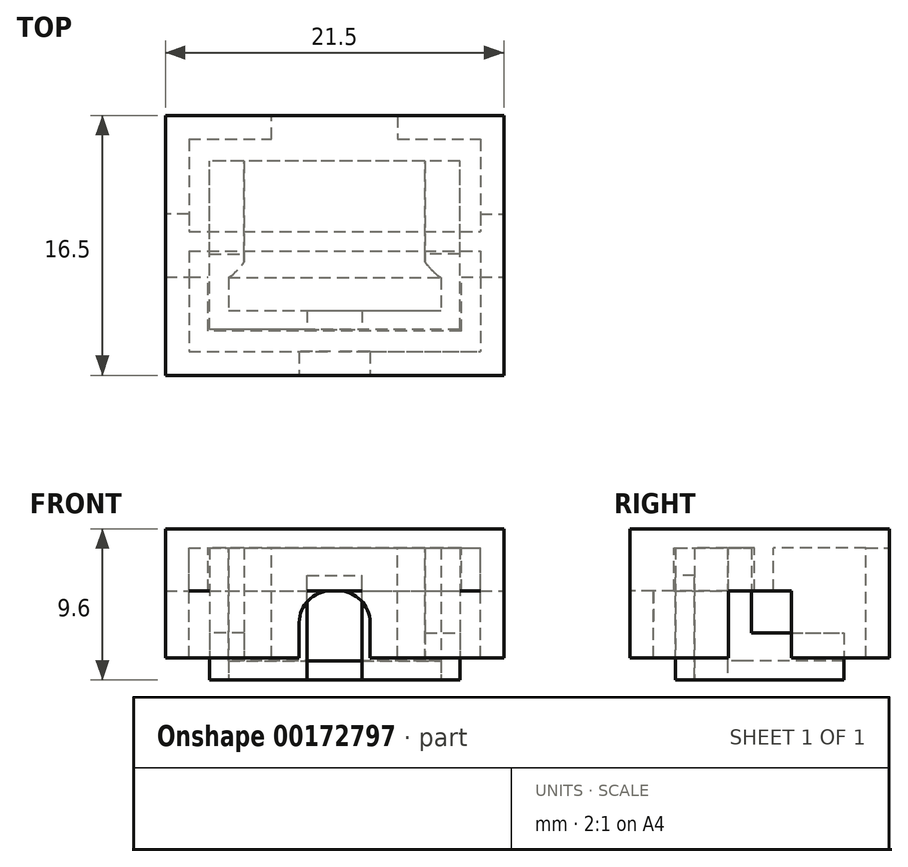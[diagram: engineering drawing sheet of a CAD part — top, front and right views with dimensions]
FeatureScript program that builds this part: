
annotation { "Feature Type Name" : "Feature", "Feature Type Description" : "" }
export const myFeature = defineFeature(function(context is Context, id is Id, definition is map)
    precondition{}
    {
        {
            var Q0;
            Q0=qCreatedBy(makeId("Top.planeOp"),FACE);
            var sketch = newSketch(context, id + "F0", { "sketchPlane" : qUnion([Q0])});
            skLineSegment(sketch, "E0.bottom", {"start": v(-6.75, 1.05) * mm, "end": v(6.75, 1.05) * mm});
            skLineSegment(sketch, "E0.top", {"start": v(-6.75, -1.05) * mm, "end": v(6.75, -1.05) * mm});
            skLineSegment(sketch, "E0.left", {"start": v(-6.75, 1.05) * mm, "end": v(-6.75, -1.05) * mm});
            skLineSegment(sketch, "E0.right", {"start": v(6.75, 1.05) * mm, "end": v(6.75, -1.05) * mm});
            skPoint(sketch, "E0.middle", {"position": v(0, 0) * mm});
            skLineSegment(sketch, "E1.bottom", {"start": v(7.95, -2.26) * mm, "end": v(-7.95, -2.26) * mm});
            skLineSegment(sketch, "E1.top", {"start": v(7.95, 8.44) * mm, "end": v(-7.95, 8.44) * mm});
            skLineSegment(sketch, "E1.left", {"start": v(7.95, -2.26) * mm, "end": v(7.95, 8.44) * mm});
            skLineSegment(sketch, "E1.right", {"start": v(-7.95, -2.26) * mm, "end": v(-7.95, 8.44) * mm});
            skPoint(sketch, "E2", {"position": v(0, -2.26) * mm});
            skLineSegment(sketch, "E3", {"start": v(-6.75, 1.05) * mm, "end": v(-6.75, 7.24) * mm});
            skLineSegment(sketch, "E4", {"start": v(-6.75, 7.24) * mm, "end": v(6.75, 7.24) * mm});
            skLineSegment(sketch, "E5", {"start": v(6.75, 7.24) * mm, "end": v(6.75, 1.05) * mm});
            skLineSegment(sketch, "E6", {"start": v(-5.75, 1.05) * mm, "end": v(-5.75, 2.55) * mm});
            skLineSegment(sketch, "E7", {"start": v(-5.75, 2.55) * mm, "end": v(-6.75, 2.55) * mm});
            skLineSegment(sketch, "E8", {"start": v(5.75, 1.05) * mm, "end": v(5.75, 2.55) * mm});
            skLineSegment(sketch, "E9", {"start": v(5.75, 2.55) * mm, "end": v(6.75, 2.55) * mm});
            skLineSegment(sketch, "E10", {"start": v(7.95, 2.55) * mm, "end": v(6.75, 2.55) * mm});
            skLineSegment(sketch, "E11", {"start": v(-7.95, 2.55) * mm, "end": v(-6.75, 2.55) * mm});
            skLineSegment(sketch, "E12", {"start": v(-5.75, 2.55) * mm, "end": v(-5.75, 8.44) * mm});
            skLineSegment(sketch, "E13", {"start": v(5.75, 2.55) * mm, "end": v(5.75, 8.44) * mm});
            skSolve(sketch);
        }
        {
            var Q0;
            Q0=makeQuery(id+"F0.imprint","IMPRINT",FACE,{"disambiguationData":[TD([[makeQuery(id+"F0.imprint","IMPRINT",EDGE,{"derivedFrom":sQuery(id+"F0.wireOp",EDGE,"E0.bottom")}),1.0]])]});
            var Q1;
            {var subQ1=sQuery(id+"F0.wireOp",EDGE,"E4");Q1=makeQuery(id+"F0.imprint","IMPRINT",FACE,{"disambiguationData":[TD([[makeQuery(id+"F0.imprint","IMPRINT",EDGE,{"derivedFrom":subQ1}),-1.0]])]});}
            var Q2;
            {var subQ4=sQuery(id+"F0.wireOp",EDGE,"E1.top");Q2=makeQuery(id+"F0.imprint","IMPRINT",FACE,{"disambiguationData":[TD([[makeQuery(id+"F0.imprint","IMPRINT",EDGE,{"derivedFrom":subQ4}),1.0]])]});}
            var Q3;
            Q3=makeQuery(id+"F0.imprint","IMPRINT",FACE,{"disambiguationData":[TD([[makeQuery(id+"F0.imprint","IMPRINT",EDGE,{"derivedFrom":sQuery(id+"F0.wireOp",EDGE,"E0.top")}),-1.0]])]});
            var Q4;
            {var subQ4=sQuery(id+"F0.wireOp",EDGE,"E11");Q4=makeQuery(id+"F0.imprint","IMPRINT",FACE,{"disambiguationData":[TD([[makeQuery(id+"F0.imprint","IMPRINT",EDGE,{"derivedFrom":subQ4}),1.0]])]});}
            var Q5;
            {var subQ7=sQuery(id+"F0.wireOp",EDGE,"E10");Q5=makeQuery(id+"F0.imprint","IMPRINT",FACE,{"disambiguationData":[TD([[makeQuery(id+"F0.imprint","IMPRINT",EDGE,{"derivedFrom":subQ7}),-1.0]])]});}
            var Q6;
            {var subQ0=sQuery(id+"F0.wireOp",EDGE,"E6");Q6=makeQuery(id+"F0.imprint","IMPRINT",FACE,{"disambiguationData":[TD([[makeQuery(id+"F0.imprint","IMPRINT",EDGE,{"derivedFrom":subQ0}),-1.0]])]});}
            extrude(context, id + "F1", {"entities" : qUnion([Q0, Q1, Q2, Q3, Q4, Q5, Q6]), "depth" : 1.21 * mm});
        }
        {
            var Q0;
            Q0=makeQuery(id+"F0.imprint","IMPRINT",FACE,{"disambiguationData":[TD([[makeQuery(id+"F0.imprint","IMPRINT",EDGE,{"derivedFrom":sQuery(id+"F0.wireOp",EDGE,"E0.top")}),-1.0]])]});
            var Q1;
            {var subQ3=sQuery(id+"F0.wireOp",EDGE,"E6");Q1=makeQuery(id+"F0.imprint","IMPRINT",FACE,{"disambiguationData":[TD([[makeQuery(id+"F0.imprint","IMPRINT",EDGE,{"derivedFrom":subQ3}),1.0]])]});}
            var Q2;
            {var subQ3=sQuery(id+"F0.wireOp",EDGE,"E8");Q2=makeQuery(id+"F0.imprint","IMPRINT",FACE,{"disambiguationData":[TD([[makeQuery(id+"F0.imprint","IMPRINT",EDGE,{"derivedFrom":subQ3}),-1.0]])]});}
            extrude(context, id + "F2", {"entities" : qUnion([Q0, Q1, Q2]), "depth" : 8.4 * mm});
        }
        {
            var Q0;
            Q0=makeQuery(id+"F1.opExtrude","SWEPT_BODY",BODY,{"disambiguationData":[OSD([sQuery(id+"F0.wireOp",EDGE,"E1.bottom"),sQuery(id+"F0.wireOp",EDGE,"E1.top"),sQuery(id+"F0.wireOp",EDGE,"E1.left"),sQuery(id+"F0.wireOp",EDGE,"E1.right")])]});
            var Q1;
            Q1=makeQuery(id+"F2.opExtrude","SWEPT_BODY",BODY,{"disambiguationData":[OSD([sQuery(id+"F0.wireOp",EDGE,"E0.bottom"),sQuery(id+"F0.wireOp",EDGE,"E0.top"),sQuery(id+"F0.wireOp",EDGE,"E0.left"),sQuery(id+"F0.wireOp",EDGE,"E0.right"),sQuery(id+"F0.wireOp",EDGE,"E1.bottom"),sQuery(id+"F0.wireOp",EDGE,"E1.left"),sQuery(id+"F0.wireOp",EDGE,"E1.right"),sQuery(id+"F0.wireOp",EDGE,"E6"),sQuery(id+"F0.wireOp",EDGE,"E7"),sQuery(id+"F0.wireOp",EDGE,"E8"),sQuery(id+"F0.wireOp",EDGE,"E9"),sQuery(id+"F0.wireOp",EDGE,"E10"),sQuery(id+"F0.wireOp",EDGE,"E11")])]});
            booleanBodies(context, id + "F3", {"operationType" : BooleanOperationType.UNION, "tools" : qUnion([Q0, Q1])});
        }
        {
            var Q0;
            Q0=makeQuery(id+"F2.opExtrude","SWEPT_FACE",FACE,{"disambiguationData":[OSD([sQuery(id+"F0.wireOp",EDGE,"E1.bottom")])]});
            var sketch = newSketch(context, id + "F4", { "sketchPlane" : qUnion([Q0])});
            skLineSegment(sketch, "E14.bottom", {"start": v(-1.75, 0) * mm, "end": v(1.75, 0) * mm});
            skLineSegment(sketch, "E14.top", {"start": v(-1.75, 6.65) * mm, "end": v(1.75, 6.65) * mm});
            skLineSegment(sketch, "E14.left", {"start": v(-1.75, 0) * mm, "end": v(-1.75, 6.65) * mm});
            skLineSegment(sketch, "E14.right", {"start": v(1.75, 0) * mm, "end": v(1.75, 6.65) * mm});
            skSolve(sketch);
        }
        {
            var Q0;
            Q0 = qSketchRegion(id + "F4", true);
            var Q1;
            Q1=makeQuery(id+"F2.opExtrude","SWEPT_FACE",FACE,{"disambiguationData":[OSD([sQuery(id+"F0.wireOp",EDGE,"E0.top")])]});
            extrude(context, id + "F5", {"entities" : qUnion([Q0]), "operationType" : NewBodyOperationType.REMOVE, "endBound" : BoundingType.UP_TO_SURFACE, "oppositeDirection" : true, "endBoundEntityFace" : qUnion([Q1]), "depth" : 25 * mm});
        }
        {
            var Q0;
            Q0=makeQuery(id+"F2.opExtrude","SWEPT_EDGE",EDGE,{"disambiguationData":[OSD([sQuery(id+"F0.wireOp",EDGE,"E0.bottom"),sQuery(id+"F0.wireOp",EDGE,"E8")])]});
            var Q1;
            Q1=makeQuery(id+"F2.opExtrude","SWEPT_EDGE",EDGE,{"disambiguationData":[OSD([sQuery(id+"F0.wireOp",EDGE,"E0.bottom"),sQuery(id+"F0.wireOp",EDGE,"E6")])]});
            fillet(context, id + "F6", {"entities" : qUnion([Q0, Q1]), "radius" : 1 * mm, "tangentPropagation" : true, "rho" : .1, "crossSection" : FilletCrossSection.CONIC, "allowEdgeOverflow" : false});
        }
        {
            var Q0;
            {var subQ5=sQuery(id+"F0.wireOp",EDGE,"E11");Q0=makeQuery(id+"F0.imprint","IMPRINT",FACE,{"disambiguationData":[TD([[makeQuery(id+"F0.imprint","IMPRINT",EDGE,{"derivedFrom":subQ5}),1.0]])]});}
            var Q1;
            {var subQ3=sQuery(id+"F0.wireOp",EDGE,"E7");Q1=makeQuery(id+"F0.imprint","IMPRINT",FACE,{"disambiguationData":[TD([[makeQuery(id+"F0.imprint","IMPRINT",EDGE,{"derivedFrom":subQ3}),-1.0]])]});}
            var Q2;
            {var subQ5=sQuery(id+"F0.wireOp",EDGE,"E9");Q2=makeQuery(id+"F0.imprint","IMPRINT",FACE,{"disambiguationData":[TD([[makeQuery(id+"F0.imprint","IMPRINT",EDGE,{"derivedFrom":subQ5}),1.0]])]});}
            var Q3;
            {var subQ9=sQuery(id+"F0.wireOp",EDGE,"E10");Q3=makeQuery(id+"F0.imprint","IMPRINT",FACE,{"disambiguationData":[TD([[makeQuery(id+"F0.imprint","IMPRINT",EDGE,{"derivedFrom":subQ9}),-1.0]])]});}
            extrude(context, id + "F7", {"entities" : qUnion([Q0, Q1, Q2, Q3]), "operationType" : NewBodyOperationType.ADD, "depth" : 3 * mm});
        }
        {
            var Q0;
            Q0=makeQuery(id+"F2.opExtrude","CAP_FACE",FACE,{"disambiguationData":[OSD([sQuery(id+"F0.wireOp",EDGE,"E0.bottom"),sQuery(id+"F0.wireOp",EDGE,"E0.top"),sQuery(id+"F0.wireOp",EDGE,"E0.left"),sQuery(id+"F0.wireOp",EDGE,"E0.right"),sQuery(id+"F0.wireOp",EDGE,"E1.bottom"),sQuery(id+"F0.wireOp",EDGE,"E1.left"),sQuery(id+"F0.wireOp",EDGE,"E1.right"),sQuery(id+"F0.wireOp",EDGE,"E6"),sQuery(id+"F0.wireOp",EDGE,"E7"),sQuery(id+"F0.wireOp",EDGE,"E8"),sQuery(id+"F0.wireOp",EDGE,"E9"),sQuery(id+"F0.wireOp",EDGE,"E10"),sQuery(id+"F0.wireOp",EDGE,"E11")])],"isStart":false});
            var sketch = newSketch(context, id + "F8", { "sketchPlane" : qUnion([Q0])});
            skLineSegment(sketch, "E15.bottom", {"start": v(-9.25, 9.84) * mm, "end": v(9.25, 9.84) * mm});
            skLineSegment(sketch, "E15.top", {"start": v(-9.25, -3.66) * mm, "end": v(-2.25, -3.66) * mm});
            skLineSegment(sketch, "E15.left", {"start": v(-9.25, 9.84) * mm, "end": v(-9.25, 5.1) * mm});
            skLineSegment(sketch, "E15.right", {"start": v(9.25, 9.84) * mm, "end": v(9.25, -3.66) * mm});
            skPoint(sketch, "E15.middle", {"position": v(0, 3.1) * mm});
            skLineSegment(sketch, "E16.0", {"start": v(-10.75, 11.34) * mm, "end": v(-10.75, -5.16) * mm});
            skLineSegment(sketch, "E16.1", {"start": v(-10.75, 11.34) * mm, "end": v(-4, 11.34) * mm});
            skLineSegment(sketch, "E16.2", {"start": v(10.75, 11.34) * mm, "end": v(10.75, -5.16) * mm});
            skLineSegment(sketch, "E16.3", {"start": v(-10.75, -5.16) * mm, "end": v(10.75, -5.16) * mm});
            skLineSegment(sketch, "E17", {"start": v(-9.25, 5.1) * mm, "end": v(-10.75, 5.1) * mm});
            skLineSegment(sketch, "E18", {"start": v(-10.75, 1.1) * mm, "end": v(-7.95, 1.1) * mm});
            skLineSegment(sketch, "E19", {"start": v(-9.25, 5.1) * mm, "end": v(-9.25, 1.1) * mm});
            skLineSegment(sketch, "E20", {"start": v(-9.25, 1.1) * mm, "end": v(-9.25, -3.66) * mm});
            skPoint(sketch, "E21", {"position": v(-9.25, 3.1) * mm});
            skLineSegment(sketch, "E22", {"start": v(9.25, 5.1) * mm, "end": v(10.75, 5.1) * mm});
            skLineSegment(sketch, "E23", {"start": v(7.95, 1.1) * mm, "end": v(10.75, 1.1) * mm});
            skLineSegment(sketch, "E24", {"start": v(-9.25, 2.55) * mm, "end": v(9.25, 2.55) * mm, "construction": true});
            skLineSegment(sketch, "E25", {"start": v(-9.25, 3.96) * mm, "end": v(9.25, 3.96) * mm});
            skLineSegment(sketch, "E26.0", {"start": v(-7.95, -2.26) * mm, "end": v(-7.95, 2.55) * mm, "construction": true});
            skLineSegment(sketch, "E26.1", {"start": v(7.95, -2.26) * mm, "end": v(-7.95, -2.26) * mm, "construction": true});
            skLineSegment(sketch, "E26.2", {"start": v(7.95, -2.26) * mm, "end": v(7.95, 2.55) * mm, "construction": true});
            skLineSegment(sketch, "E27", {"start": v(-4, 9.84) * mm, "end": v(-4, 11.34) * mm});
            skLineSegment(sketch, "E28", {"start": v(4, 11.34) * mm, "end": v(4, 9.84) * mm});
            skLineSegment(sketch, "E29", {"start": v(-4, 11.34) * mm, "end": v(4, 11.34) * mm});
            skLineSegment(sketch, "E30", {"start": v(4, 11.34) * mm, "end": v(10.75, 11.34) * mm});
            skPoint(sketch, "E31", {"position": v(0, 11.34) * mm});
            skPoint(sketch, "E32.orphan", {"position": v(-9.25, 1.1) * mm});
            skPoint(sketch, "E33.orphan", {"position": v(9.25, 1.1) * mm});
            skLineSegment(sketch, "E34", {"start": v(-2.25, -3.66) * mm, "end": v(2.25, -3.66) * mm});
            skLineSegment(sketch, "E35", {"start": v(2.25, -3.66) * mm, "end": v(9.25, -3.66) * mm});
            skPoint(sketch, "E36", {"position": v(0, -3.66) * mm});
            skLineSegment(sketch, "E37.0", {"start": v(-9.25, 2.75) * mm, "end": v(9.25, 2.75) * mm});
            skLineSegment(sketch, "E38.0", {"start": v(-8.05, -2.36) * mm, "end": v(-8.05, 2.55) * mm});
            skLineSegment(sketch, "E38.1", {"start": v(8.05, -2.36) * mm, "end": v(-8.05, -2.36) * mm});
            skLineSegment(sketch, "E38.2", {"start": v(8.05, -2.36) * mm, "end": v(8.05, 2.55) * mm});
            skSolve(sketch);
        }
        {
            var Q0;
            {var subQ6=sQuery(id+"F8.wireOp",EDGE,"E15.top");Q0=makeQuery(id+"F8.imprint","IMPRINT",FACE,{"disambiguationData":[TD([[makeQuery(id+"F8.imprint","IMPRINT",EDGE,{"derivedFrom":subQ6}),-1.0]])]});}
            var Q1;
            {var subQ1=sQuery(id+"F8.wireOp",EDGE,"E15.left");Q1=makeQuery(id+"F8.imprint","IMPRINT",FACE,{"disambiguationData":[TD([[makeQuery(id+"F8.imprint","IMPRINT",EDGE,{"derivedFrom":subQ1}),-1.0]])]});}
            var Q2;
            {var subQ0=sQuery(id+"F8.wireOp",EDGE,"E22");Q2=makeQuery(id+"F8.imprint","IMPRINT",FACE,{"disambiguationData":[TD([[makeQuery(id+"F8.imprint","IMPRINT",EDGE,{"derivedFrom":subQ0}),1.0]])]});}
            var Q3;
            {var subQ5=sQuery(id+"F8.wireOp",EDGE,"J5TBD8wA-XzV8-tCQy-03cy-WX8Owma7t69J");Q3=makeQuery(id+"F8.imprint","IMPRINT",FACE,{"disambiguationData":[TD([[makeQuery(id+"F8.imprint","IMPRINT",EDGE,{"derivedFrom":subQ5}),-1.0]])]});}
            var Q4;
            Q4=makeQuery(id+"F1.opExtrude","CAP_FACE",FACE,{"disambiguationData":[OSD([sQuery(id+"F0.wireOp",EDGE,"E0.bottom"),sQuery(id+"F0.wireOp",EDGE,"E0.top"),sQuery(id+"F0.wireOp",EDGE,"E0.left"),sQuery(id+"F0.wireOp",EDGE,"E0.right"),sQuery(id+"F0.wireOp",EDGE,"E1.bottom"),sQuery(id+"F0.wireOp",EDGE,"E1.top"),sQuery(id+"F0.wireOp",EDGE,"E1.left"),sQuery(id+"F0.wireOp",EDGE,"E1.right")])],"isStart":false});
            extrude(context, id + "F9", {"entities" : qUnion([Q0, Q1, Q2, Q3]), "oppositeDirection" : true, "endBoundEntityFace" : qUnion([Q4]), "depth" : 7 * mm});
        }
        {
            var Q0;
            {var subQ0=sQuery(id+"F8.wireOp",EDGE,"E38.1");Q0=makeQuery(id+"F8.imprint","IMPRINT",FACE,{"disambiguationData":[TD([[makeQuery(id+"F8.imprint","IMPRINT",EDGE,{"derivedFrom":subQ0}),-1.0]])]});}
            var Q1;
            {var subQ2=sQuery(id+"F8.wireOp",EDGE,"E37.0");Q1=makeQuery(id+"F8.imprint","IMPRINT",FACE,{"disambiguationData":[TD([[makeQuery(id+"F8.imprint","IMPRINT",EDGE,{"derivedFrom":subQ2}),-1.0]])]});}
            var Q2;
            {var subQ11=sQuery(id+"F0.wireOp",EDGE,"E0.top");Q2=makeQuery(id+"F8.imprint","IMPRINT",FACE,{"disambiguationData":[TD([[makeQuery(id+"F8.imprint","IMPRINT",EDGE,{"derivedFrom":makeQuery(id+"F2.opExtrude","CAP_EDGE",EDGE,{"disambiguationData":[OSD([subQ11])],"isStart":false})}),-1.0]])]});}
            var Q3;
            {var subQ1=sQuery(id+"F8.wireOp",EDGE,"E17");Q3=makeQuery(id+"F8.imprint","IMPRINT",FACE,{"disambiguationData":[TD([[makeQuery(id+"F8.imprint","IMPRINT",EDGE,{"derivedFrom":subQ1}),1.0]])]});}
            var Q4;
            Q4=makeQuery(id+"F8.imprint","IMPRINT",FACE,{"disambiguationData":[TD([[makeQuery(id+"F8.imprint","IMPRINT",EDGE,{"derivedFrom":sQuery(id+"F8.wireOp",EDGE,"E15.top")}),-1.0]])]});
            var Q5;
            Q5=makeQuery(id+"F8.imprint","IMPRINT",FACE,{"disambiguationData":[TD([[makeQuery(id+"F8.imprint","IMPRINT",EDGE,{"derivedFrom":sQuery(id+"F8.wireOp",EDGE,"E15.top")}),1.0]])]});
            var Q6;
            {var subQ0=sQuery(id+"F8.wireOp",EDGE,"E22");Q6=makeQuery(id+"F8.imprint","IMPRINT",FACE,{"disambiguationData":[TD([[makeQuery(id+"F8.imprint","IMPRINT",EDGE,{"derivedFrom":subQ0}),-1.0]])]});}
            var Q7;
            {var subQ0=sQuery(id+"F8.wireOp",EDGE,"E25");Q7=makeQuery(id+"F8.imprint","IMPRINT",FACE,{"disambiguationData":[TD([[makeQuery(id+"F8.imprint","IMPRINT",EDGE,{"derivedFrom":subQ0}),-1.0]])]});}
            var Q8;
            {var subQ0=sQuery(id+"F8.wireOp",EDGE,"E15.left");Q8=makeQuery(id+"F8.imprint","IMPRINT",FACE,{"disambiguationData":[TD([[makeQuery(id+"F8.imprint","IMPRINT",EDGE,{"derivedFrom":subQ0}),1.0]])]});}
            var Q9;
            {var subQ1=sQuery(id+"F8.wireOp",EDGE,"E15.left");Q9=makeQuery(id+"F8.imprint","IMPRINT",FACE,{"disambiguationData":[TD([[makeQuery(id+"F8.imprint","IMPRINT",EDGE,{"derivedFrom":subQ1}),-1.0]])]});}
            var Q10;
            {var subQ0=sQuery(id+"F8.wireOp",EDGE,"E27");Q10=makeQuery(id+"F8.imprint","IMPRINT",FACE,{"disambiguationData":[TD([[makeQuery(id+"F8.imprint","IMPRINT",EDGE,{"derivedFrom":subQ0}),-1.0]])]});}
            var Q11;
            {var subQ0=sQuery(id+"F8.wireOp",EDGE,"E22");Q11=makeQuery(id+"F8.imprint","IMPRINT",FACE,{"disambiguationData":[TD([[makeQuery(id+"F8.imprint","IMPRINT",EDGE,{"derivedFrom":subQ0}),1.0]])]});}
            extrude(context, id + "F10", {"entities" : qUnion([Q0, Q1, Q2, Q3, Q4, Q5, Q6, Q7, Q8, Q9, Q10, Q11]), "operationType" : NewBodyOperationType.ADD, "depth" : 1.2 * mm});
        }
        {
            var Q0;
            {var subQ1=sQuery(id+"F8.wireOp",EDGE,"E17");Q0=makeQuery(id+"F8.imprint","IMPRINT",FACE,{"disambiguationData":[TD([[makeQuery(id+"F8.imprint","IMPRINT",EDGE,{"derivedFrom":subQ1}),1.0]])]});}
            var Q1;
            {var subQ0=sQuery(id+"F8.wireOp",EDGE,"E25");Q1=makeQuery(id+"F8.imprint","IMPRINT",FACE,{"disambiguationData":[TD([[makeQuery(id+"F8.imprint","IMPRINT",EDGE,{"derivedFrom":subQ0}),-1.0]])]});}
            var Q2;
            {var subQ0=sQuery(id+"F8.wireOp",EDGE,"E22");Q2=makeQuery(id+"F8.imprint","IMPRINT",FACE,{"disambiguationData":[TD([[makeQuery(id+"F8.imprint","IMPRINT",EDGE,{"derivedFrom":subQ0}),-1.0]])]});}
            var Q3;
            Q3=makeQuery(id+"F8.imprint","IMPRINT",FACE,{"disambiguationData":[TD([[makeQuery(id+"F8.imprint","IMPRINT",EDGE,{"derivedFrom":sQuery(id+"F8.wireOp",EDGE,"E15.top")}),1.0]])]});
            extrude(context, id + "F11", {"entities" : qUnion([Q0, Q1, Q2, Q3]), "operationType" : NewBodyOperationType.ADD, "oppositeDirection" : true, "depth" : 2.75 * mm});
        }
        {
            var Q0;
            {var subQ0=sQuery(id+"F8.wireOp",EDGE,"E16.3");Q0=makeQuery(id+"F10.boolean.opBoolean","MERGE",FACE,{"derivedFrom":[makeQuery(id+"F9.opExtrude","SWEPT_FACE",FACE,{"disambiguationData":[OSD([subQ0])]}),makeQuery(id+"F10.opExtrude","SWEPT_FACE",FACE,{"disambiguationData":[OSD([subQ0])]})]});}
            var sketch = newSketch(context, id + "F12", { "sketchPlane" : qUnion([Q0])});
            skLineSegment(sketch, "E39.0", {"start": v(-1.75, 0) * mm, "end": v(-1.75, 6.65) * mm, "construction": true});
            skLineSegment(sketch, "E39.1", {"start": v(1.75, 0) * mm, "end": v(1.75, 6.65) * mm, "construction": true});
            skLineSegment(sketch, "E39.2", {"start": v(-1.75, 6.65) * mm, "end": v(1.75, 6.65) * mm, "construction": true});
            skLineSegment(sketch, "E40.bottom", {"start": v(-2.25, 1.4) * mm, "end": v(2.25, 1.4) * mm});
            skLineSegment(sketch, "E40.top", {"start": v(-0.25, 5.65) * mm, "end": v(0.25, 5.65) * mm});
            skLineSegment(sketch, "E40.left", {"start": v(-2.25, 1.4) * mm, "end": v(-2.25, 3.65) * mm});
            skLineSegment(sketch, "E40.right", {"start": v(2.25, 1.4) * mm, "end": v(2.25, 3.65) * mm});
            skPoint(sketch, "E41", {"position": v(0, 1.4) * mm});
            skPoint(sketch, "E42.visualSharp", {"position": v(-2.25, 5.65) * mm});
            skArc(sketch, "E42.filletArc", {"start": v(-0.25, 5.65) * mm, "mid": v(-1.66, 5.06) * mm, "end": v(-2.25, 3.65) * mm});
            skPoint(sketch, "E43.visualSharp", {"position": v(2.25, 5.65) * mm});
            skArc(sketch, "E43.filletArc", {"start": v(2.25, 3.65) * mm, "mid": v(1.66, 5.06) * mm, "end": v(0.25, 5.65) * mm});
            skSolve(sketch);
        }
        {
            var Q0;
            Q0 = qSketchRegion(id + "F12", true);
            var Q1;
            Q1=makeQuery(id+"F11.opExtrude","SWEPT_FACE",FACE,{"disambiguationData":[OSD([sQuery(id+"F8.wireOp",EDGE,"E38.1")])]});
            extrude(context, id + "F13", {"entities" : qUnion([Q0]), "operationType" : NewBodyOperationType.REMOVE, "endBound" : BoundingType.UP_TO_SURFACE, "oppositeDirection" : true, "endBoundEntityFace" : qUnion([Q1]), "depth" : 25 * mm});
        }
    });
